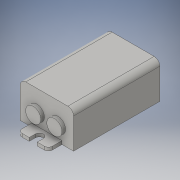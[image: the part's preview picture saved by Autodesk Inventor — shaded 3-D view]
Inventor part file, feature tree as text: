
AUTODESK INVENTOR PART (.ipt)
format: ipt  version: 2016 (Build 200138000, 138)  size: 182,272 bytes
history: native  units: in
note: dims shown in document units (in); Inventor stores cm internally (conversion verified against a paired STEP export)
features: extrude x3, fillet x3, sketch x3
ambient origin geometry x8: Origin, YZ Plane, XZ Plane, XY Plane, X Axis, Y Axis, Z Axis, Center Point
bodies: Solid1 (feature_tree)
feature tree (9):
  extrude  "Extrusion1"  Depth=1.176in
  fillet  "Fillet1"  Radius=0.795in
  extrude  "Extrusion2"  Depth=0.255in
  fillet  "Fillet2"  Radius=0.3in
  fillet  "Fillet3"  Radius=0.245in
  extrude  "Extrusion3"  Depth=0.245in
  sketch  "Sketch1"  dims[d0=1.9in d1=1.176in d2=0.795in d3=0.0in]
  sketch  "Sketch2"  dims[d4=0.125in d5=0.255in d6=0.3in d7=0.245in]
  sketch  "Sketch3"  dims[d9=0.176in d10=0.245in d11=0.3in d12=1.176in d13=0.176in d15=0.255in d16=0.255in d17=0.255in d18=0.073in d19=0.0in d20=0.088in d21=0.088in d22=0.334in d23=0.334in d24=0.326in d25=0.326in d26=0.466in d27=0.176in d28=0.2in d29=0.079in d30=1.979in d31=0.0in d32=0.0in]
